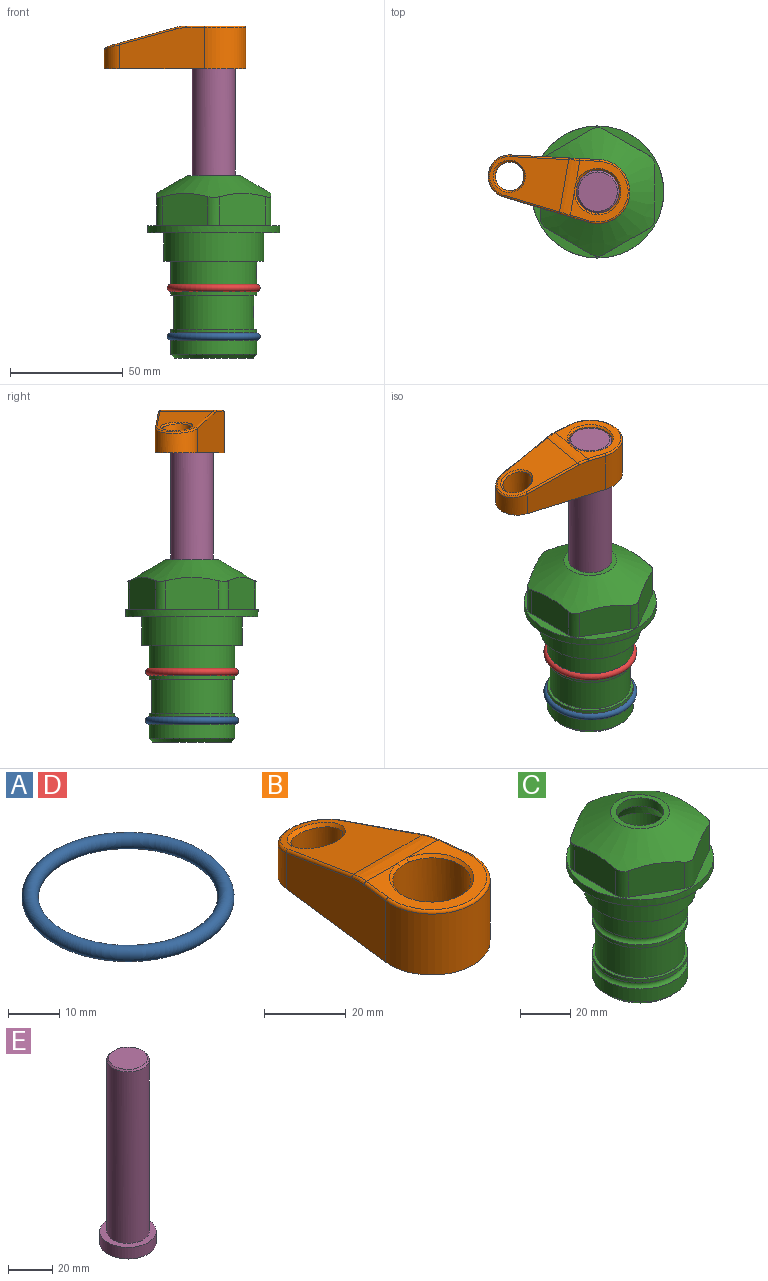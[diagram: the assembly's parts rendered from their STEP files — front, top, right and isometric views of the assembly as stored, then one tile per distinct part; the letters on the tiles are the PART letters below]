
ASSEMBLY  parts=5 mates=4
PART A: 1 faces, bbox 44.7x44.7x3.2 mm
  f0: torus R=19.05mm, axis (0,0,1), area 1193.9mm2
PART B: 31 faces, bbox 31.7x65.5x19.8 mm
  f0: plane 39.12x18.26mm, normal (0.99,0.12,0), area 612.2mm2, adj f1,f4,f7,f11,f13,f15
  f1: cylinder r=9.53mm len=18.91mm, axis (0,0,-1), area 296.1mm2, adj f0,f2,f7,f17
  f2: plane 39.12x18.26mm, normal (-0.99,0.12,0), area 612.2mm2, adj f1,f4,f7,f12,f14,f16
  f3: cylinder r=6.35mm len=12.7mm, axis (0,0,-1), area 362.4mm2, adj f7,f18
  f4: cylinder r=14.29mm len=28.58mm, axis (0,0,-1), area 882.2mm2, adj f0,f2,f7,f10
  f5: cylinder r=9.53mm len=19.05mm, axis (0,0,-1), area 1092.6mm2, adj f7,f19,f20
  f6: plane 26.99x23.69mm, normal (0,0,1), area 216.2mm2, adj f9,f10,f11,f12,f19
  f7: plane 63.5x28.58mm, normal (0,0,-1), area 661.8mm2, adj f0,f1,f2,f3,f4,f5,f22,f23
  f8: plane 33.52x23.6mm, normal (0,0.26,0.97), area 486mm2, adj f9,f15,f16,f17,f18
  f9: cylinder r=19.05mm len=24.72mm, axis (1,0,0), area 120.4mm2, adj f6,f8,f13,f14,f20
  f10: torus R=13.49mm, axis (0,0,1), area 59mm2, adj f4,f6,f11,f12
  f11: cylinder r=0.79mm len=8.67mm, axis (0.12,-0.99,0), area 10.8mm2, adj f0,f6,f10,f13
  f12: cylinder r=0.79mm len=8.67mm, axis (0.12,0.99,0), area 10.8mm2, adj f2,f6,f10,f14
  f13: bspline ~4.95x1.42mm, area 6.1mm2, adj f0,f9,f11,f15
  f14: bspline ~4.95x1.42mm, area 6.1mm2, adj f2,f9,f12,f16
  f15: cylinder r=0.79mm len=25.95mm, axis (0.12,-0.96,0.26), area 32.9mm2, adj f0,f8,f13,f17
  f16: cylinder r=0.79mm len=25.95mm, axis (0.12,0.96,-0.26), area 32.9mm2, adj f2,f8,f14,f17
  f17: bspline ~18.91x8.38mm, area 30mm2, adj f1,f8,f15,f16
  f18: bspline ~14.29x14.29mm, area 48.3mm2, adj f3,f8
  f19: cone r=9.53mm half-angle=45deg, axis (0,0,1), area 66.5mm2, adj f5,f6,f20
  f20: bspline ~3.22x0.96mm, area 3.5mm2, adj f5,f9,f19
  f21: plane 2.75x2.72mm, normal (0,0,-1), area 2.9mm2, adj f23,f25,f28
  f22: plane 23.05x15.88mm, normal (-0.99,-0.12,0), area 323.6mm2, adj f7,f25,f26,f27,f28,f29
  f23: plane 23.05x15.88mm, normal (0.99,-0.12,0), area 323.6mm2, adj f7,f21,f25,f27,f28,f30
  f24: cylinder r=9.53mm len=10.69mm, axis (0,0,-1), area 114.7mm2, adj f7,f27,f29,f30
  f25: cylinder r=12.7mm len=20.59mm, axis (0,0,-1), area 381.1mm2, adj f7,f21,f22,f23,f26,f28
  f26: plane 2.75x2.72mm, normal (0,0,-1), area 2.9mm2, adj f22,f25,f28
  f27: plane 19.72x18.37mm, normal (0,-0.26,-0.97), area 291.8mm2, adj f22,f23,f24,f28,f29,f30
  f28: cylinder r=15.88mm len=19.92mm, axis (1,0,0), area 54.8mm2, adj f21,f22,f23,f25,f26,f27
  f29: cylinder r=1.59mm len=11mm, axis (0,0,-1), area 34.7mm2, adj f7,f22,f24,f27
  f30: cylinder r=1.59mm len=11mm, axis (0,0,-1), area 34.7mm2, adj f7,f23,f24,f27
PART C: 36 faces, bbox 58.7x58.7x81 mm
  f0: cylinder r=17.78mm len=35.56mm, axis (0,0,1), area 1670.8mm2, adj f23,f24,f31
  f1: cylinder r=19.05mm len=38.1mm, axis (0,0,1), area 1191.9mm2, adj f26,f27,f30
  f2: plane 58.66x58.66mm, normal (0,0,-1), area 1150.6mm2, adj f3,f28
  f3: cylinder r=29.33mm len=58.66mm, axis (0,0,-1), area 585.1mm2, adj f2,f4
  f4: plane 58.66x58.66mm, normal (0,0,1), area 475.9mm2, adj f3,f5,f6,f7,f8,f9,f10,f11
  f5: plane 20.32x14.34mm, normal (-0.5,0.87,0), area 324.4mm2, adj f4,f15,f16,f17
  f6: plane 20.32x14.34mm, normal (0.5,0.87,0), area 324.4mm2, adj f4,f14,f15,f17
  f7: plane 23.48x14.34mm, normal (1,0,0), area 324.4mm2, adj f4,f13,f14,f17
  f8: plane 20.32x14.34mm, normal (0.5,-0.87,0), area 324.4mm2, adj f4,f12,f13,f17
  f9: plane 20.32x14.34mm, normal (-0.5,-0.87,0), area 324.4mm2, adj f4,f11,f12,f17
  f10: plane 23.48x14.34mm, normal (-1,0,0), area 324.4mm2, adj f4,f11,f16,f17
  f11: cylinder r=5.08mm len=12.85mm, axis (0,0,-1), area 67.2mm2, adj f4,f9,f10,f17
  f12: cylinder r=5.08mm len=12.85mm, axis (0,0,-1), area 67.2mm2, adj f4,f8,f9,f17
  f13: cylinder r=5.08mm len=12.85mm, axis (0,0,-1), area 67.2mm2, adj f4,f7,f8,f17
  f14: cylinder r=5.08mm len=12.85mm, axis (0,0,-1), area 67.2mm2, adj f4,f6,f7,f17
  f15: cylinder r=5.08mm len=12.85mm, axis (0,0,-1), area 67.2mm2, adj f4,f5,f6,f17
  f16: cylinder r=5.08mm len=12.85mm, axis (0,0,-1), area 67.2mm2, adj f4,f5,f10,f17
  f17: cone r=11.73mm half-angle=60deg, axis (0,0,-1), area 2071.8mm2, adj f5,f6,f7,f8,f9,f10,f11,f12
  f18: plane 23.46x23.46mm, normal (0,0,1), area 147.4mm2, adj f17,f35
  f19: plane 34.93x34.93mm, normal (0,0,-1), area 958mm2, adj f29
  f20: cylinder r=19.05mm len=38.1mm, axis (0,0,1), area 760.1mm2, adj f21,f29
  f21: torus R=19.05mm, axis (0,0,1), area 565.3mm2, adj f20,f22
  f22: cylinder r=19.05mm len=38.1mm, axis (0,0,1), area 190mm2, adj f21,f23
  f23: plane 38.1x38.1mm, normal (0,0,1), area 146.9mm2, adj f0,f22
  f24: plane 38.1x38.1mm, normal (0,0,-1), area 146.9mm2, adj f0,f25
  f25: cylinder r=19.05mm len=38.1mm, axis (0,0,1), area 190mm2, adj f24,f26
  f26: torus R=19.05mm, axis (0,0,1), area 565.3mm2, adj f1,f25
  f27: plane 44.45x44.45mm, normal (0,0,-1), area 411.7mm2, adj f1,f28
  f28: cylinder r=22.23mm len=44.45mm, axis (0,0,1), area 1773.5mm2, adj f2,f27
  f29: cone r=19.05mm half-angle=45deg, axis (0,0,1), area 257.5mm2, adj f19,f20
  f30: cylinder r=3.17mm len=6.75mm, axis (-1,0,0), area 128mm2, adj f1,f33
  f31: cylinder r=3.17mm len=6.35mm, axis (-1,0,0), area 102.5mm2, adj f0,f33
  f32: plane 25.4x25.4mm, normal (0,0,1), area 506.7mm2, adj f33
  f33: cylinder r=12.7mm len=66.42mm, axis (0,0,-1), area 5236.2mm2, adj f30,f31,f32,f34
  f34: cone r=9.53mm half-angle=30deg, axis (0,0,-1), area 443.4mm2, adj f33,f35
  f35: cylinder r=9.53mm len=19.05mm, axis (0,0,-1), area 240.9mm2, adj f18,f34
PART D: same geometry as A
PART E: 6 faces, bbox 25.4x25.4x101.6 mm
  f0: plane 17.46x17.46mm, normal (0,0,1), area 239.5mm2, adj f5
  f1: plane 25.4x25.4mm, normal (0,0,-1), area 506.7mm2, adj f2
  f2: cylinder r=12.7mm len=25.4mm, axis (0,0,1), area 506.7mm2, adj f1,f3
  f3: plane 25.4x25.4mm, normal (0,0,1), area 221.7mm2, adj f2,f4
  f4: cylinder r=9.53mm len=94.46mm, axis (0,0,1), area 5653mm2, adj f3,f5
  f5: cone r=8.73mm half-angle=45deg, axis (0,0,-1), area 64.4mm2, adj f0,f4
PLACE A t=(0,0,-21.59)mm
PLACE B rot(axis=(0,0,1),80.1deg) t=(0,0,28.35)mm
PLACE C at identity fixed
PLACE D at identity
PLACE E rot(axis=(0,0,1),80.1deg) t=(0,0,27.55)mm
MATE fastened A.f0 <-> C.f0  axis (0,0,1) through (0,0,-46.1)mm
MATE fastened D.f0 <-> C.f0  axis (0,0,1) through (0,0,-24.51)mm
MATE cylindrical E.f2 <-> C.f0  axis (0,0,-1) through (0,0,-10.55)mm
MATE fastened B.f4 <-> E.f2  axis (0,0,1) through (0,0,91.05)mm
